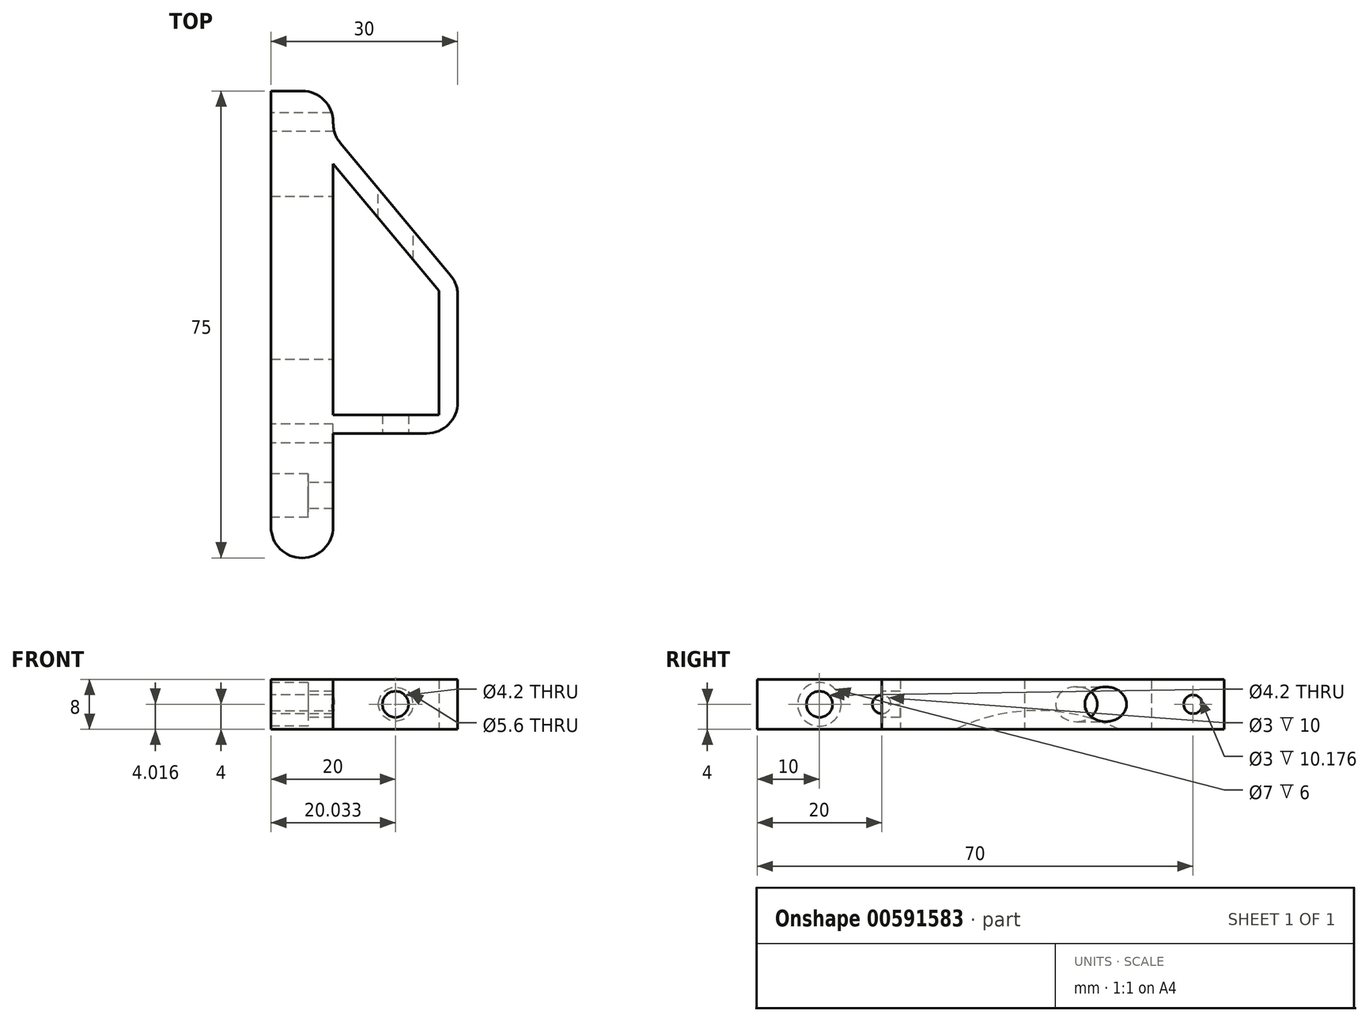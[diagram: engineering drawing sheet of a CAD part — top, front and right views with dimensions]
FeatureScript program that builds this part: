
annotation { "Feature Type Name" : "Feature", "Feature Type Description" : "" }
export const myFeature = defineFeature(function(context is Context, id is Id, definition is map)
    precondition{}
    {
        {
            var Q0;
            Q0=qCreatedBy(makeId("Top.planeOp"),FACE);
            var sketch = newSketch(context, id + "F0", { "sketchPlane" : qUnion([Q0])});
            skLineSegment(sketch, "E0", {"start": v(0, 5) * mm, "end": v(0, -70) * mm});
            skLineSegment(sketch, "E1", {"start": v(0, -70) * mm, "end": v(5, -70) * mm});
            skLineSegment(sketch, "E2", {"start": v(5, -70) * mm, "end": v(5, -50) * mm});
            skLineSegment(sketch, "E3", {"start": v(5, -50) * mm, "end": v(25, -50) * mm});
            skLineSegment(sketch, "E4", {"start": v(25, -50) * mm, "end": v(25, -26) * mm});
            skLineSegment(sketch, "E5", {"start": v(5, -47) * mm, "end": v(5, 5) * mm});
            skLineSegment(sketch, "E6", {"start": v(5, -6.69) * mm, "end": v(22, -27.09) * mm});
            skLineSegment(sketch, "E7", {"start": v(22, -27.09) * mm, "end": v(22, -47) * mm});
            skLineSegment(sketch, "E8", {"start": v(22, -47) * mm, "end": v(5, -47) * mm});
            skLineSegment(sketch, "E9", {"start": v(0, 5) * mm, "end": v(5, 5) * mm});
            skLineSegment(sketch, "E10", {"start": v(5, -2) * mm, "end": v(25, -26) * mm});
            skLineSegment(sketch, "E11", {"start": v(5, -50) * mm, "end": v(5, -47) * mm});
            skSolve(sketch);
        }
        {
            var Q0;
            Q0=makeQuery(id+"F0.imprint","IMPRINT",FACE,{"disambiguationData":[TD([[makeQuery(id+"F0.imprint","IMPRINT",EDGE,{"derivedFrom":sQuery(id+"F0.wireOp",EDGE,"E3")}),1.0]])]});
            var Q1;
            Q1=makeQuery(id+"F0.imprint","IMPRINT",FACE,{"disambiguationData":[TD([[makeQuery(id+"F0.imprint","IMPRINT",EDGE,{"derivedFrom":sQuery(id+"F0.wireOp",EDGE,"E0")}),1.0]])]});
            extrude(context, id + "F1", {"entities" : qUnion([Q0, Q1]), "depth" : 8 * mm, "offsetDistance" : 25 * mm});
        }
        {
            var Q0;
            Q0=makeQuery(id+"F1.opExtrude","SWEPT_FACE",FACE,{"disambiguationData":[OSD([sQuery(id+"F0.wireOp",EDGE,"E3")])]});
            var sketch = newSketch(context, id + "F2", { "sketchPlane" : qUnion([Q0])});
            skCircle(sketch, "E12", {"center": v(15, 4) * mm, "radius": 2.1 * mm});
            skPoint(sketch, "E13", {"position": v(25, 4) * mm});
            skSolve(sketch);
        }
        {
            var Q0;
            Q0=makeQuery(id+"F2.imprint","IMPRINT",FACE,{"disambiguationData":[TD([[makeQuery(id+"F2.imprint","IMPRINT",EDGE,{"derivedFrom":sQuery(id+"F2.wireOp",EDGE,"E12")}),1.0]])]});
            extrude(context, id + "F3", {"entities" : qUnion([Q0]), "operationType" : NewBodyOperationType.REMOVE, "endBound" : BoundingType.THROUGH_ALL, "oppositeDirection" : true, "depth" : 25 * mm, "offsetDistance" : 25 * mm});
        }
        {
            var Q0;
            Q0=qCreatedBy(makeId("Front.planeOp"),FACE);
            var sketch = newSketch(context, id + "F4", { "sketchPlane" : qUnion([Q0])});
            skCircle(sketch, "E14", {"center": v(15.03, 4.02) * mm, "radius": 2.8 * mm});
            skSolve(sketch);
        }
        {
            var Q0;
            Q0 = qSketchRegion(id + "F4", true);
            extrude(context, id + "F5", {"entities" : qUnion([Q0]), "operationType" : NewBodyOperationType.REMOVE, "depth" : 25 * mm, "offsetDistance" : 25 * mm});
        }
        {
            var Q0;
            {var subQ0=sQuery(id+"F0.wireOp",EDGE,"E0");Q0=makeQuery(id+"FQQC2h0txBZHMMr_1.boolean.opBoolean","MERGE",FACE,{"derivedFrom":[makeQuery(id+"F1.opExtrude","SWEPT_FACE",FACE,{"disambiguationData":[OSD([subQ0])]}),makeQuery(id+"FQQC2h0txBZHMMr_1.opExtrude","SWEPT_FACE",FACE,{"disambiguationData":[OSD([subQ0])]})]});}
            extrude(context, id + "F6", {"entities" : qUnion([Q0]), "operationType" : NewBodyOperationType.ADD, "depth" : 5 * mm, "offsetDistance" : 25 * mm});
        }
        {
            var Q0;
            {var subQ0=sQuery(id+"F0.wireOp",EDGE,"E0");Q0=makeQuery(id+"F6.boolean.opBoolean","MERGE",FACE,{"derivedFrom":[makeQuery(id+"F1.opExtrude","CAP_FACE",FACE,{"disambiguationData":[OSD([subQ0,sQuery(id+"F0.wireOp",EDGE,"E1"),sQuery(id+"F0.wireOp",EDGE,"E2"),sQuery(id+"F0.wireOp",EDGE,"E3"),sQuery(id+"F0.wireOp",EDGE,"E4"),sQuery(id+"F0.wireOp",EDGE,"E5"),sQuery(id+"F0.wireOp",EDGE,"E6"),sQuery(id+"F0.wireOp",EDGE,"E7"),sQuery(id+"F0.wireOp",EDGE,"E8"),sQuery(id+"F0.wireOp",EDGE,"E9"),sQuery(id+"F0.wireOp",EDGE,"E10")])],"isStart":true}),makeQuery(id+"F6.opExtrude","SWEPT_FACE",FACE,{"disambiguationData":[OSD([subQ0]),TDD([makeQuery(id+"F1.opExtrude","CAP_EDGE",EDGE,{"disambiguationData":[OSD([subQ0])],"isStart":true})])]})]});}
            var sketch = newSketch(context, id + "F7", { "sketchPlane" : qUnion([Q0])});
            skLineSegment(sketch, "E15.bottom", {"start": v(-5, 70) * mm, "end": v(0, 70) * mm});
            skLineSegment(sketch, "E15.top", {"start": v(-5, -5) * mm, "end": v(0, -5) * mm});
            skLineSegment(sketch, "E15.left", {"start": v(-5, 70) * mm, "end": v(-5, -5) * mm});
            skLineSegment(sketch, "E15.right", {"start": v(0, 70) * mm, "end": v(0, -5) * mm});
            skSolve(sketch);
        }
        {
            var Q0;
            Q0=makeQuery(id+"FNwgnSww7YgQ5T7_1.boolean.opBoolean","MERGE",FACE,{"derivedFrom":[makeQuery(id+"F6.opExtrude","CAP_FACE",FACE,{"disambiguationData":[OSD([sQuery(id+"F0.wireOp",EDGE,"E0")])],"isStart":false}),makeQuery(id+"FNwgnSww7YgQ5T7_1.opExtrude","SWEPT_FACE",FACE,{"disambiguationData":[OSD([sQuery(id+"F7.wireOp",EDGE,"E15.left")])]})]});
            var sketch = newSketch(context, id + "F8", { "sketchPlane" : qUnion([Q0])});
            skCircle(sketch, "E16", {"center": v(0, 4) * mm, "radius": 1.5 * mm});
            skCircle(sketch, "E17", {"center": v(50, 4) * mm, "radius": 1.5 * mm});
            skLineSegment(sketch, "E18", {"start": v(70, 4) * mm, "end": v(-5, 4) * mm, "construction": true});
            skPoint(sketch, "E18.endSnap0", {"position": v(-5, 0) * mm});
            skCircle(sketch, "E19", {"center": v(60, 4) * mm, "radius": 2.1 * mm});
            skCircle(sketch, "E20", {"center": v(60, 4) * mm, "radius": 3.5 * mm});
            skSolve(sketch);
        }
        {
            var Q0;
            Q0=makeQuery(id+"F8.imprint","IMPRINT",FACE,{"disambiguationData":[TD([[makeQuery(id+"F8.imprint","IMPRINT",EDGE,{"derivedFrom":sQuery(id+"F8.wireOp",EDGE,"E16")}),1.0]])]});
            var Q1;
            Q1=makeQuery(id+"F8.imprint","IMPRINT",FACE,{"disambiguationData":[TD([[makeQuery(id+"F8.imprint","IMPRINT",EDGE,{"derivedFrom":sQuery(id+"F8.wireOp",EDGE,"E17")}),1.0]])]});
            var Q2;
            Q2=makeQuery(id+"F8.imprint","IMPRINT",FACE,{"disambiguationData":[TD([[makeQuery(id+"F8.imprint","IMPRINT",EDGE,{"derivedFrom":sQuery(id+"F8.wireOp",EDGE,"E19")}),1.0]])]});
            var Q3;
            Q3=makeQuery(id+"F1.opExtrude","SWEPT_FACE",FACE,{"disambiguationData":[OSD([sQuery(id+"F0.wireOp",EDGE,"E2")])]});
            extrude(context, id + "F9", {"entities" : qUnion([Q0, Q1, Q2]), "operationType" : NewBodyOperationType.REMOVE, "endBound" : BoundingType.UP_TO_SURFACE, "oppositeDirection" : true, "depth" : 25 * mm, "endBoundEntityFace" : qUnion([Q3]), "offsetDistance" : 25 * mm});
        }
        {
            var Q0;
            Q0=makeQuery(id+"F8.imprint","IMPRINT",FACE,{"disambiguationData":[TD([[makeQuery(id+"F8.imprint","IMPRINT",EDGE,{"derivedFrom":sQuery(id+"F8.wireOp",EDGE,"E19")}),-1.0]])]});
            extrude(context, id + "F10", {"entities" : qUnion([Q0]), "operationType" : NewBodyOperationType.REMOVE, "oppositeDirection" : true, "depth" : 6 * mm, "offsetDistance" : 25 * mm});
        }
        {
            var Q0;
            Q0=makeQuery(id+"F1.opExtrude","SWEPT_EDGE",EDGE,{"disambiguationData":[OSD([sQuery(id+"F0.wireOp",EDGE,"E5"),sQuery(id+"F0.wireOp",EDGE,"E9")])]});
            var Q1;
            Q1=makeQuery(id+"F1.opExtrude","SWEPT_EDGE",EDGE,{"disambiguationData":[OSD([sQuery(id+"F0.wireOp",EDGE,"E1"),sQuery(id+"F0.wireOp",EDGE,"E2")])]});
            var Q2;
            Q2=makeQuery(id+"F1.opExtrude","SWEPT_EDGE",EDGE,{"disambiguationData":[OSD([sQuery(id+"F0.wireOp",EDGE,"E4"),sQuery(id+"F0.wireOp",EDGE,"E10")])]});
            var Q3;
            Q3=makeQuery(id+"F1.opExtrude","SWEPT_EDGE",EDGE,{"disambiguationData":[OSD([sQuery(id+"F0.wireOp",EDGE,"E3"),sQuery(id+"F0.wireOp",EDGE,"E4")])]});
            var Q4;
            Q4=makeQuery(id+"F1.opExtrude","SWEPT_EDGE",EDGE,{"disambiguationData":[OSD([sQuery(id+"F0.wireOp",EDGE,"E5"),sQuery(id+"F0.wireOp",EDGE,"E10")])]});
            var Q5;
            Q5=makeQuery(id+"FNwgnSww7YgQ5T7_1.boolean.opBoolean","MERGE",EDGE,{"derivedFrom":[makeQuery(id+"F6.opExtrude","CAP_EDGE",EDGE,{"disambiguationData":[OSD([sQuery(id+"F0.wireOp",EDGE,"E0"),sQuery(id+"F0.wireOp",EDGE,"E1")])],"isStart":false}),makeQuery(id+"FNwgnSww7YgQ5T7_1.opExtrude","SWEPT_EDGE",EDGE,{"disambiguationData":[OSD([sQuery(id+"F7.wireOp",EDGE,"E15.bottom"),sQuery(id+"F7.wireOp",EDGE,"E15.left")])]})]});
            fillet(context, id + "F11", {"entities" : qUnion([Q0, Q1, Q2, Q3, Q4, Q5]), "radius" : 5 * mm, "tangentPropagation" : true, "allowEdgeOverflow" : false});
        }
        {
            var Q0;
            Q0=qCreatedBy(makeId("Right.planeOp"),FACE);
            var sketch = newSketch(context, id + "F12", { "sketchPlane" : qUnion([Q0])});
            skCircle(sketch, "E21", {"center": v(-25, -27) * mm, "radius": 30 * mm});
            skSolve(sketch);
        }
        {
            var Q0;
            Q0 = qSketchRegion(id + "F12", true);
            extrude(context, id + "F13", {"entities" : qUnion([Q0]), "operationType" : NewBodyOperationType.REMOVE, "oppositeDirection" : true, "depth" : 18 * mm, "offsetDistance" : 25 * mm, "symmetric" : true});
        }
    });
